# Revit family: QF_MACOM_CH09E-DA
name_source: partatom
category: Equipamento especial
units: mm (PartAtom-declared; Revit-internal decimal feet)

## family parameters
Com base no plano de trabalho = Não
Compartilhado = Não
Corte com vazios quando carregada = Não
Cota do conector redondo = Utilizar diâmetro
Número OmniClass = 23.40.40.14.17.14
Ponto de cálculo do ambiente = Não
Sempre na vertical = Sim
Tipo de parte = Normal
Título OmniClass = Hot Plates

## types (2) — shared parameters
Depth = 686,000 mm
Descrição = CHAPA EXPORTACAO MACOM 915, DUPLO GAS
Elevação padrão = 0,000 mm
Fabricante = MACOM
Gas Connection Height = 60,000 mm
Gas Pressure = 0,0 bar
Gas Size = 3/4"
Height = 404,000 mm
Modelo = CH09E-DA
Plate Depth = 520,000 mm
Plate Width = 911,000 mm
Show Clearances = Sim
URL = https://www.acosmacom.com.br
Volume = 0,25 m³
Weight = 92,00 kg
Width = 915,000 mm

## per-type parameters (varying)
| type | Gas Consumption GLP | Gas Consumption GN | Gas Input GLP | Gas Input GN |
| CH09E-G | 1,52 Kg/h | 0,0 m³/h | 69515 Btu/h |  |
| CH09E-N |  | 1,9 m³/h | 0 Btu/h | 17519 Kcal/h |

## geometry (parser evidence)
native form markers: Sweep x1
no freeform markers — native parametric forms only
